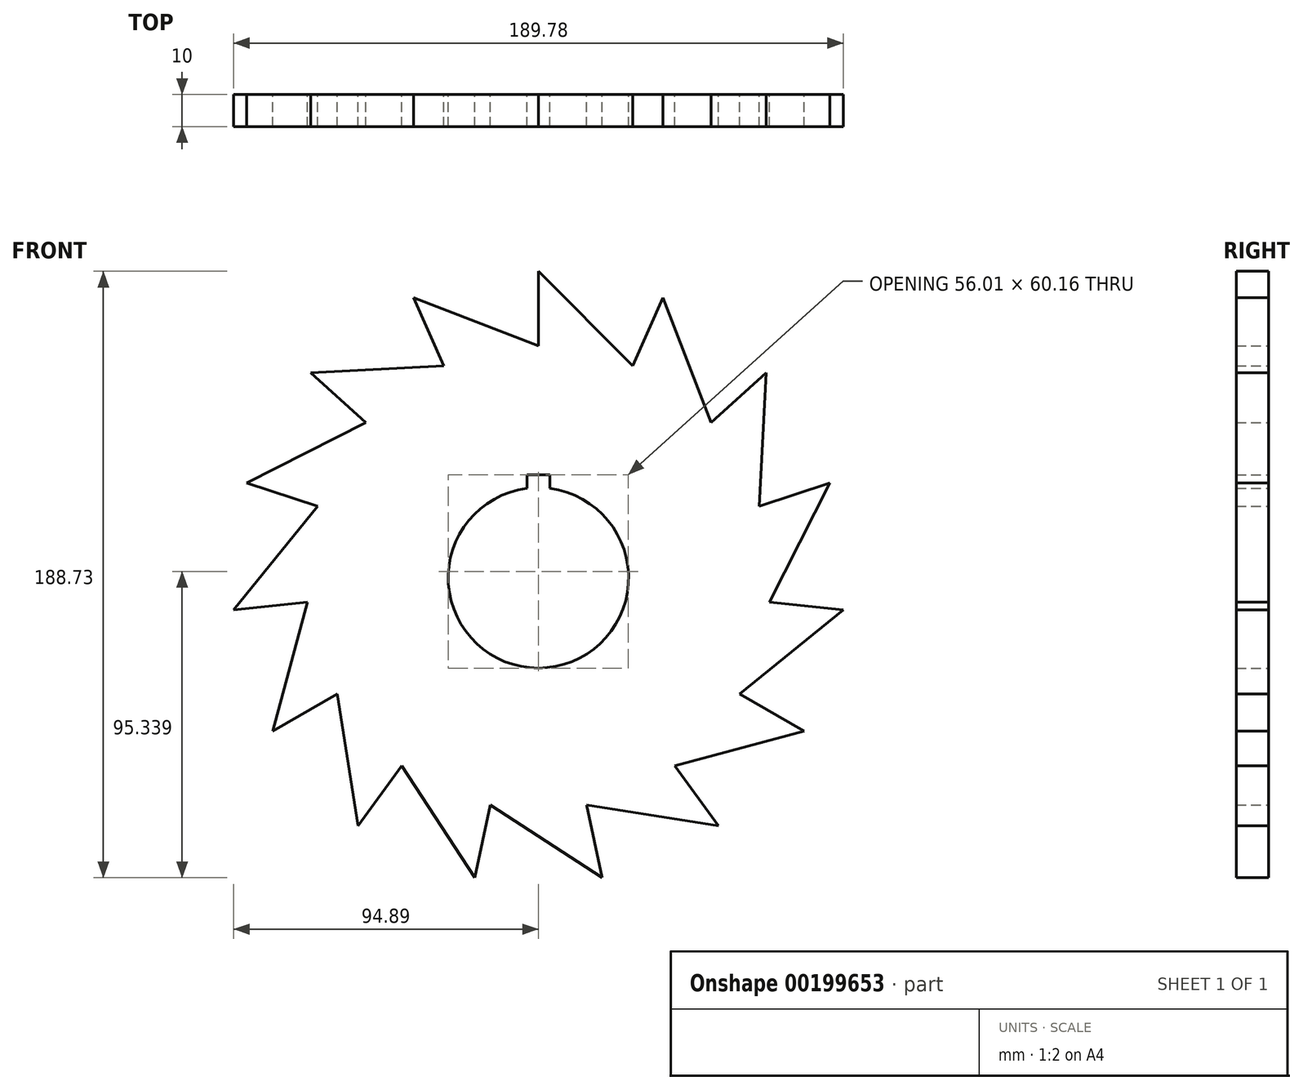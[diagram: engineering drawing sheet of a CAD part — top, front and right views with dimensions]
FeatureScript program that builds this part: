
annotation { "Feature Type Name" : "Feature", "Feature Type Description" : "" }
export const myFeature = defineFeature(function(context is Context, id is Id, definition is map)
    precondition{}
    {
        {
            var Q0;
            Q0=qCreatedBy(makeId("Front.planeOp"),FACE);
            var sketch = newSketch(context, id + "F0", { "sketchPlane" : qUnion([Q0])});
            skArc(sketch, "E0", {"start": v(-3.58, 27.83) * mm, "mid": v(0, -28.06) * mm, "end": v(3.58, 27.83) * mm});
            skCircle(sketch, "E1", {"center": v(0, 0) * mm, "radius": 72.23 * mm});
            skLineSegment(sketch, "E2", {"start": v(0, 95.4) * mm, "end": v(29.47, 65.94) * mm});
            skLineSegment(sketch, "E3.bottom", {"start": v(3.58, 32.1) * mm, "end": v(-3.58, 32.1) * mm});
            skLineSegment(sketch, "E3.left", {"start": v(3.58, 32.1) * mm, "end": v(3.58, 27.83) * mm});
            skLineSegment(sketch, "E3.right", {"start": v(-3.58, 32.1) * mm, "end": v(-3.58, 27.83) * mm});
            skPoint(sketch, "E3.middle", {"position": v(0, 28.06) * mm});
            skLineSegment(sketch, "E4.trimOffspring", {"start": v(0, 72.23) * mm, "end": v(0, 95.4) * mm});
            skLineSegment(sketch, "E5.1.0", {"start": v(-38.8, 87.16) * mm, "end": v(0.1, 72.23) * mm});
            skLineSegment(sketch, "E5.1.1", {"start": v(-29.38, 65.98) * mm, "end": v(-38.8, 87.16) * mm});
            skLineSegment(sketch, "E5.2.0", {"start": v(-70.9, 63.84) * mm, "end": v(-29.29, 66.02) * mm});
            skLineSegment(sketch, "E5.2.1", {"start": v(-53.67, 48.33) * mm, "end": v(-70.9, 63.84) * mm});
            skLineSegment(sketch, "E5.3.0", {"start": v(-90.74, 29.48) * mm, "end": v(-53.6, 48.4) * mm});
            skLineSegment(sketch, "E5.3.1", {"start": v(-68.7, 22.32) * mm, "end": v(-90.74, 29.48) * mm});
            skLineSegment(sketch, "E5.4.0", {"start": v(-94.89, -9.97) * mm, "end": v(-68.66, 22.41) * mm});
            skLineSegment(sketch, "E5.4.1", {"start": v(-71.83, -7.55) * mm, "end": v(-94.89, -9.97) * mm});
            skLineSegment(sketch, "E5.5.0", {"start": v(-82.63, -47.7) * mm, "end": v(-71.84, -7.45) * mm});
            skLineSegment(sketch, "E5.5.1", {"start": v(-62.55, -36.11) * mm, "end": v(-82.63, -47.7) * mm});
            skLineSegment(sketch, "E5.6.0", {"start": v(-56.08, -77.19) * mm, "end": v(-62.6, -36.03) * mm});
            skLineSegment(sketch, "E5.6.1", {"start": v(-42.45, -58.43) * mm, "end": v(-56.08, -77.19) * mm});
            skLineSegment(sketch, "E5.7.0", {"start": v(-19.84, -93.32) * mm, "end": v(-42.53, -58.37) * mm});
            skLineSegment(sketch, "E5.7.1", {"start": v(-15.02, -70.65) * mm, "end": v(-19.84, -93.32) * mm});
            skLineSegment(sketch, "E5.8.0", {"start": v(19.84, -93.32) * mm, "end": v(-15.11, -70.63) * mm});
            skLineSegment(sketch, "E5.8.1", {"start": v(15.02, -70.65) * mm, "end": v(19.84, -93.32) * mm});
            skLineSegment(sketch, "E5.9.0", {"start": v(56.08, -77.19) * mm, "end": v(14.92, -70.67) * mm});
            skLineSegment(sketch, "E5.9.1", {"start": v(42.45, -58.43) * mm, "end": v(56.08, -77.19) * mm});
            skLineSegment(sketch, "E5.10.0", {"start": v(82.63, -47.7) * mm, "end": v(42.37, -58.5) * mm});
            skLineSegment(sketch, "E5.10.1", {"start": v(62.55, -36.11) * mm, "end": v(82.63, -47.7) * mm});
            skLineSegment(sketch, "E5.11.0", {"start": v(94.89, -9.97) * mm, "end": v(62.5, -36.2) * mm});
            skLineSegment(sketch, "E5.11.1", {"start": v(71.83, -7.55) * mm, "end": v(94.89, -9.97) * mm});
            skLineSegment(sketch, "E5.12.0", {"start": v(90.74, 29.48) * mm, "end": v(71.82, -7.65) * mm});
            skLineSegment(sketch, "E5.12.1", {"start": v(68.7, 22.32) * mm, "end": v(90.74, 29.48) * mm});
            skLineSegment(sketch, "E5.13.0", {"start": v(70.9, 63.84) * mm, "end": v(68.72, 22.22) * mm});
            skLineSegment(sketch, "E5.13.1", {"start": v(53.67, 48.33) * mm, "end": v(70.9, 63.84) * mm});
            skLineSegment(sketch, "E5.14.0", {"start": v(38.8, 87.16) * mm, "end": v(53.74, 48.25) * mm});
            skLineSegment(sketch, "E5.14.1", {"start": v(29.38, 65.98) * mm, "end": v(38.8, 87.16) * mm});
            skSolve(sketch);
        }
        {
            var Q0;
            Q0 = qSketchRegion(id + "F0", true);
            var Q1;
            Q1=makeQuery(id+"F0.imprint","IMPRINT",FACE,{"disambiguationData":[TD([[makeQuery(id+"F0.imprint","IMPRINT",EDGE,{"derivedFrom":sQuery(id+"F0.wireOp",EDGE,"E0")}),-1.0]])]});
            extrude(context, id + "F1", {"entities" : qUnion([Q0, Q1]), "depth" : 10 * mm});
        }
    });
